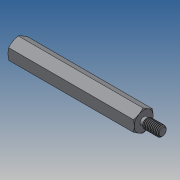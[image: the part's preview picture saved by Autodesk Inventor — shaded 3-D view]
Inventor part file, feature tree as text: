
AUTODESK INVENTOR PART (.ipt)
format: ipt  version: 2018.3 (Build 223284000, 284)  size: 589,824 bytes
history: native  units: in
note: dims shown in document units (in); Inventor stores cm internally (conversion verified against a paired STEP export)
features: extrude x1
ambient origin geometry x8: Origin, YZ Plane, XZ Plane, XY Plane, X Axis, Y Axis, Z Axis, Center Point
bodies: Solid1 (feature_tree)
feature tree (1):
  extrude  "Extrude8"  [1 undecoded]
note: 1 required parameter value undecoded (feature->parameter linkage not recoverable at this tier; creation-order binding heuristic only, values carry confidence <= 0.55)
